# Revit family: 81802129(2021)
name_source: partatom
category: Plumbing Fixtures
units: mm (PartAtom-declared; Revit-internal decimal feet)

## family parameters
Always vertical = Yes
Cut with Voids When Loaded = No
OmniClass Number = 23.45.55.00
OmniClass Title = Sanitary Faucets, Wastes
Part Type = Normal
Room Calculation Point = No
Round Connector Dimension = Use Diameter
Shared = No
Work Plane-Based = No

## types (1)
- 81802129 Cover part for washbasin faucet, 3 V, Bluetooth
    2D/3D/BIM Files URL = http://static.hansa.com
    3D View = https://static.hansa.com
    Advanced Features = Software settings adjustable via App
    Aerator = Standard aerator;PCA® - constant flow rate regardless of pressure variations
    Afterflow Period = 3 s (1-20 s)
    AssetType = Fixed
    Automatic Flush Frequency = off (off/1-120 h)
    Automatic Flush Period = 30 s (1-1800 s)
    BIMObjectName = 81802129(2021)
    Backflow Prevention EN1717 = AA
    Battery = AA 1.5 V Lithium x 2
    Bluetooth = 5.x (D060576)
    BodyMaterial = Brass
    Brand = HANSA
    CWFU = 0
    Catalog Drawing URL = http://static.hansa.com
    CloseOffRating = 0
    Color = Chrome
    Concealed Parts = Round rosette
    Connection = One inlet for cold or premixed water
    Default Elevation = 0 mm  [stored 0 ft]
    Dimension Drawing URL = http://static.hansa.com
    DurationUnit = Year
    EAN Number = 4057304016905
    EMC Directive = Radio Equipment Directive 2014/53/EU , 
Low Voltage Directive 2014/35/EU , 
EMC Directive 2014/30/EU , 
RoHS Directive 2011/65/EU
    EN Standard = EN 15091,
ETSI EN 301 489-1 V1.9.2 , 
ETSI EN 300 328 v2.2.2 , 
EN 61000-6-1:2007 , 
EN 61000-6-3:2007+A1:2011+AC:2012 , 
EN 60335-1:2012+A11+A13+A1+A14+A2+A15:2021, Part 19.11.4
    ETIM Class Number = EC010340 Electronic tap
    Electrical Connection = 12 V
    Electronic Parts = Autofocus infrared sensor;Solenoid valve;External control unit;Light indicated function(s);Low battery indicator
    Excluded Items = Without transformer
    FDV Document URL = http://www.hansa.com
    FaucetMainMaterial = Brass
    Features = Trim Kit;Touchless;Battery-operated;External transformer;Bluetooth®
    Finish = Polished
    Flow Drawing URL = http://static.hansa.com
    Flow Rate At 300kPa With Flow Controller = 0.1 L/s
    FlowCoefficient = 0
    Group = Washbasin faucet
    IfcExportAs = IfcValveType
    IfcExportType = FAUCET
    Installation Type = Concealed wall mounting
    Installation and Maintenance Guide URL = http://static.hansa.com
    Interactive AR View URL = https://static.hansa.com
    Manufacturer = HANSA
    ManufacturerName = HANSA
    ManufacturerURL = http://www.hansa.com
    Market = International;Germany;Austria;Belgium;Netherlands;France;Czech Republic;Slovakia;Italy;Spain
    Material = Brass
    Max Flow Period = 2 min (1 - 1800 s)
    Max. Hot Water Supply = 70 °C
    Mechanical Parts = Litter filter(s)
    Mobile Product Information URL = http://mpi.hansa.com
    Model = 81802129 Cover part for washbasin faucet, 3 V, Bluetooth
    ModelReference = 81802129
    NBSDescription = Water supply fittings for wash basins and troughs
    NBSReference = 45-35-70/371
    Name = 81802129 Cover part for washbasin faucet, 3 V, Bluetooth
    Name_en = 81802129 Cover part for washbasin faucet, 3 V, Bluetooth
    Noise Class = I (ISO 3822)
    NominalDepth = 325 mm
    NominalHeight = 170 mm  [stored 0.557743 ft]
    NominalWidth = 170 mm  [stored 0.557743 ft]
    Operating Distance = 10-310 mm (140-330 mm)
    Operating Voltage = 312 V
    Product Code = 81802129
    Product Family = HANSAELECTRA
    Product Image URL = http://static.hansa.com
    Product URL = http://static.hansa.com
    Protection Class = IP 55
    Sales Package dimensions (LxWxH) = 370 x 192 x 90
    Shape = Sculptured
    Size = 170x170x325 mm
    Spare-Part Information URL = http://static.hansa.com
    Spout Projection = 310 mm
    Surface treatment = Chrome
    Technical DataSheet URL = http://www.hansa.com
    UNSPSC Class Number = 30181700 Faucets or taps
    URL Declaration Of Performance (DOP) = http://static.hansa.com
    URL Declaration of Asbestos = http://static.hansa.com
    URL Declaration of Conformity = http://static.hansa.com
    URL Declaration of SCIP = http://static.hansa.com
    URL EU Packaging Declaration = http://static.hansa.com
    URL EcoLabel Declaration = http://static.hansa.com
    URL REACH = http://static.hansa.com
    URL UN38.3 = http://static.hansa.com
    URL UWL = http://static.hansa.com
    URL WEEE = http://static.hansa.com
    Uniclass2 = Pr_40_30_96_96
    Uniclass2015Description = Washbasin manual water supply sets
    Uniclass2015Reference = Pr_40_20_87_96
    Version = 1
    VersionDate = 01/06/2023
    Warranty Information URL = http://warranty.hansa.com
    WarrantyDescription = http://warranty.hansa.com
    WarrantyDurationUnit = Year
    Working Pressure = 100 - 1000 kPa

note: [stored X ft] marks values corroborated as IEEE doubles in the binary element streams (Revit-internal decimal feet)

## geometry (parser evidence)
native form markers: Sweep x5
no freeform markers — native parametric forms only
